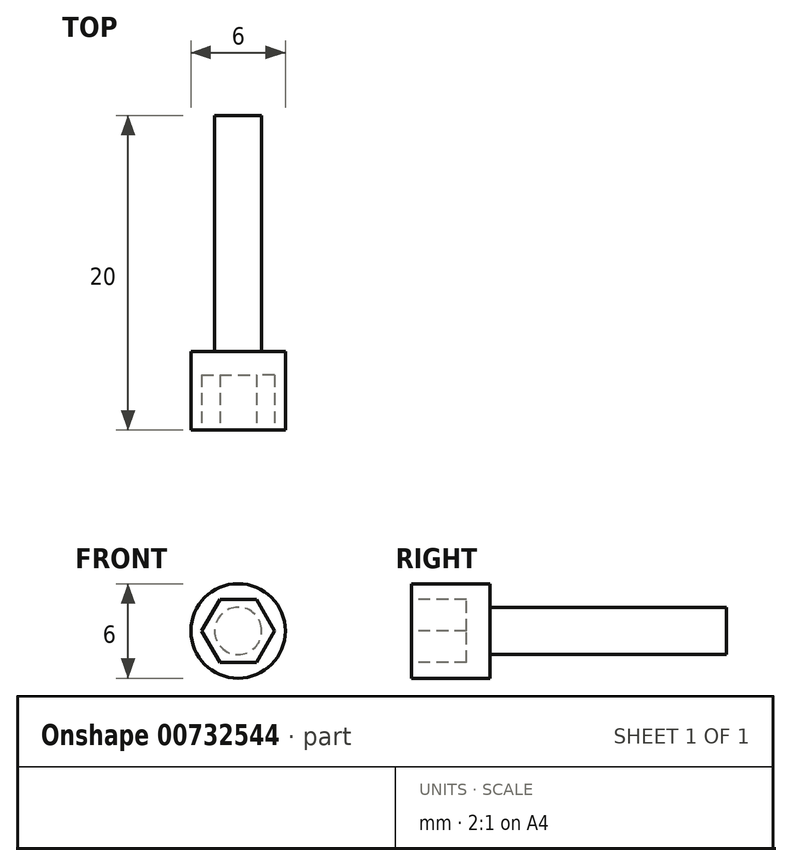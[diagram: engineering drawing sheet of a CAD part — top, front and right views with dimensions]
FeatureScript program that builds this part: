
annotation { "Feature Type Name" : "Feature", "Feature Type Description" : "" }
export const myFeature = defineFeature(function(context is Context, id is Id, definition is map)
    precondition{}
    {
        {
            var Q0;
            Q0=qCreatedBy(makeId("Front.planeOp"),FACE);
            var sketch = newSketch(context, id + "F0", { "sketchPlane" : qUnion([Q0])});
            skCircle(sketch, "E0", {"center": v(0, 0) * mm, "radius": 3 * mm});
            skSolve(sketch);
        }
        {
            var Q0;
            Q0 = qSketchRegion(id + "F0", true);
            extrude(context, id + "F1", {"entities" : qUnion([Q0]), "depth" : 5 * mm, "offsetDistance" : 25 * mm});
        }
        {
            var Q0;
            Q0=makeQuery(id+"F1.opExtrude","CAP_FACE",FACE,{"disambiguationData":[OSD([sQuery(id+"F0.wireOp",EDGE,"E0")])],"isStart":false});
            var sketch = newSketch(context, id + "F2", { "sketchPlane" : qUnion([Q0])});
            skCircle(sketch, "E1.cCircle", {"center": v(0, 0) * mm, "radius": 2 * mm, "construction": true});
            skLineSegment(sketch, "E1.0", {"start": v(-1.15, 2) * mm, "end": v(1.15, 2) * mm});
            skLineSegment(sketch, "E1.1", {"start": v(1.15, 2) * mm, "end": v(2.3, 0) * mm});
            skLineSegment(sketch, "E1.2", {"start": v(2.3, 0) * mm, "end": v(1.15, -2) * mm});
            skLineSegment(sketch, "E1.3", {"start": v(1.15, -2) * mm, "end": v(-1.15, -2) * mm});
            skLineSegment(sketch, "E1.4", {"start": v(-1.15, -2) * mm, "end": v(-2.3, 0) * mm});
            skLineSegment(sketch, "E1.5", {"start": v(-2.3, 0) * mm, "end": v(-1.15, 2) * mm});
            skPoint(sketch, "E1.0.midPoint", {"position": v(0, 2) * mm});
            skSolve(sketch);
        }
        {
            var Q0;
            Q0 = qSketchRegion(id + "F2", true);
            extrude(context, id + "F3", {"entities" : qUnion([Q0]), "operationType" : NewBodyOperationType.REMOVE, "oppositeDirection" : true, "depth" : 3.5 * mm, "offsetDistance" : 25 * mm});
        }
        {
            var Q0;
            Q0=makeQuery(id+"F1.opExtrude","CAP_FACE",FACE,{"disambiguationData":[OSD([sQuery(id+"F0.wireOp",EDGE,"E0")])],"isStart":true});
            var sketch = newSketch(context, id + "F4", { "sketchPlane" : qUnion([Q0])});
            skCircle(sketch, "E2", {"center": v(0, 0) * mm, "radius": 1.5 * mm});
            skSolve(sketch);
        }
        {
            var Q0;
            Q0 = qSketchRegion(id + "F4", true);
            extrude(context, id + "F5", {"entities" : qUnion([Q0]), "operationType" : NewBodyOperationType.ADD, "depth" : 15 * mm, "offsetDistance" : 25 * mm});
        }
    });
